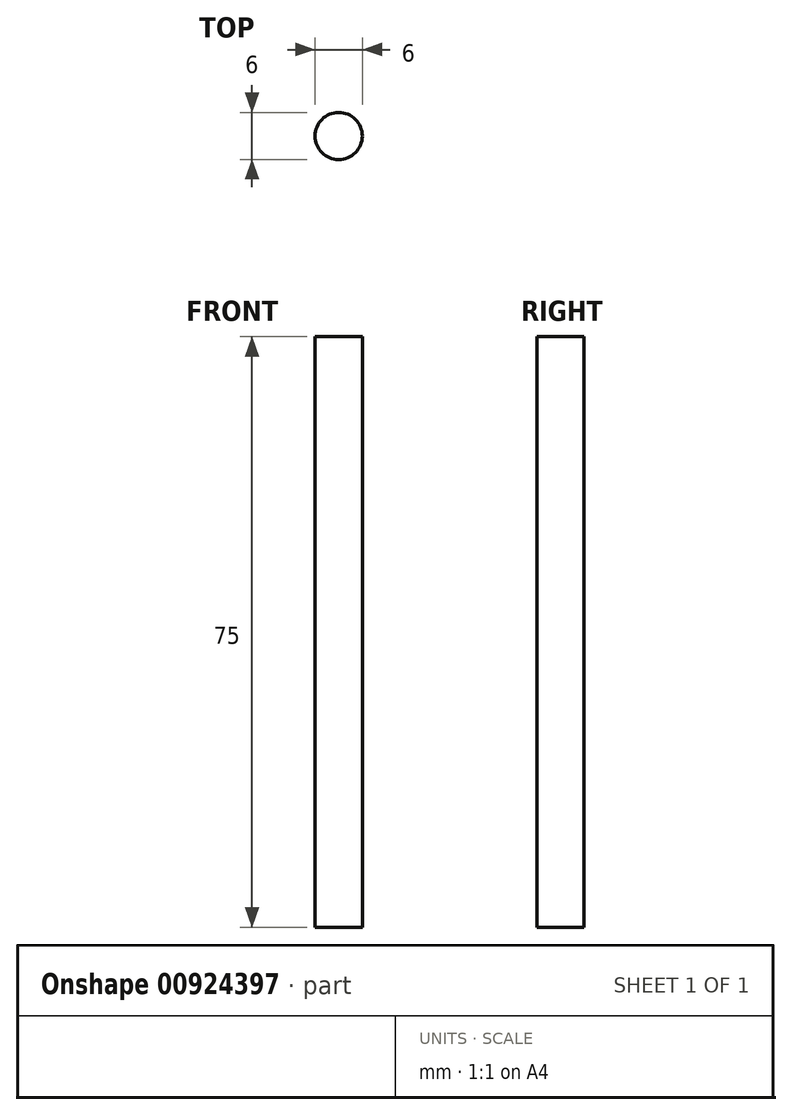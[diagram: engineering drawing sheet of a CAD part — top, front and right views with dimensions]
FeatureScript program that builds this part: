
annotation { "Feature Type Name" : "Feature", "Feature Type Description" : "" }
export const myFeature = defineFeature(function(context is Context, id is Id, definition is map)
    precondition{}
    {
        {
            var Q0;
            Q0=qCreatedBy(makeId("Top.planeOp"),FACE);
            var sketch = newSketch(context, id + "F0", { "sketchPlane" : qUnion([Q0])});
            skCircle(sketch, "E0", {"center": v(-34.57, 32.03) * mm, "radius": 3 * mm});
            skSolve(sketch);
        }
        {
            var Q0;
            Q0 = qSketchRegion(id + "F0", true);
            extrude(context, id + "F1", {"entities" : qUnion([Q0]), "depth" : 75 * mm, "offsetDistance" : 25 * mm});
        }
    });
